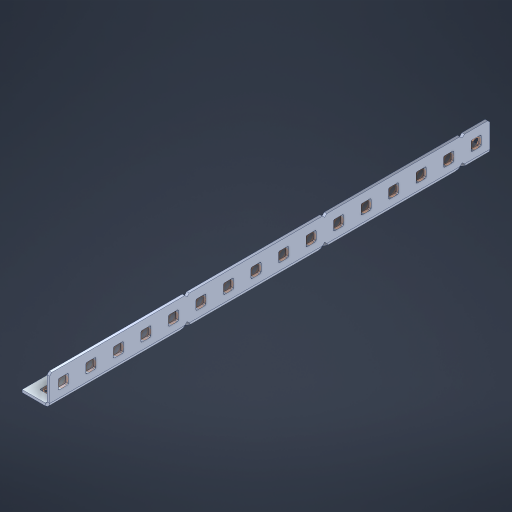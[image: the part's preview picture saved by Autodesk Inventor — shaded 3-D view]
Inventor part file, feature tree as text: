
AUTODESK INVENTOR PART (.ipt)
format: ipt  version: 2023 (Build 270158000, 158)  size: 676,864 bytes
history: native  units: in
note: dims shown in document units (in); Inventor stores cm internally (conversion verified against a paired STEP export)
features: other x37, extrude x31, sheet_metal_op x10, sketch x8, mirror x1, pattern_linear x1, chamfer x1
ambient origin geometry x8: Origin, YZ Plane, XZ Plane, XY Plane, X Axis, Y Axis, Z Axis, Center Point
bodies: Solid1 (feature_tree), Body (feature_tree)
feature tree (89):
  other  "Flange Pattern Plane"
  sheet_metal_op  "Flange Pattern"
  sheet_metal_op  "Body Pattern"
  other  "Arc Length"
  mirror  "Notch Mirror"
  pattern_linear  "Notch Pattern"  Spacing1=0.1875in  [1 undecoded]
  chamfer  "End Chamfer"
  extrude  "Half Cut"  Depth=0.0469in
  sketch  "Sketch1"  dims[d0=2.5in]
  other  "Plate1"
  sketch  "Sketch2"  dims[d1=8.0in]
  other  "Plate2"
  sheet_metal_op  "Bend1"
  sheet_metal_op  "Corner1"
  sketch  "Sketch3"  dims[d2=0.0469in]
  other  "Flange Pattern Sketch"
  sketch  "Sketch7"  dims[d3=0.0469in]
  other  "Srf1"
  other  "Srf2"
  sketch  "Sketch8"  dims[d4=0.0234in]
  sketch  "Sketch9"  dims[d5=0.0938in]
  other  "Srf91"
  sheet_metal_op  "Body Pattern Sketch"
  other  "Srf92"
  sketch  "Sketch13"  dims[d6=0.0469in]
  sketch  "Sketch14"  dims[d7=0.5in d8=90.0deg d9=0.0312in d10=0.1875in d11=0.0469in d12=0.0469in d16=0.182in d17=0.02in d18=0.0469in d19=0.0in d20=0.25in d21=0.25in d46=0.172in d47=1.0in d48=0.0in d49=0.182in d50=0.02in d51=0.25in d52=0.25in d53=0.0469in d54=0.0in d55=0.172in d56=1.0in d57=0.0in d60=6.2992in d62=0.5in d63=0.3937in d65=0.5in d85=0.1227in d86=0.1659in d88=0.04in d89=0.0469in d90=0.0in d91=0.04in d92=0.0491in d95=2.5in d96=0.04in d97=0.25in d98=45.0deg d101=0.0in d102=2.497in d131=0.5in d132=6.2992in d134=0.5in d139=0.5in]
  other  "Srf856"
  other  "Srf1310"
  other  "Srf1311"
  other  "Srf1312"
  other  "Srf1376"
  other  "Srf1377"
  other  "Srf1728"
  other  "Srf1755"
  other  "Srf1878"
  other  "Srf1879"
  other  "Srf1880"
  other  "Srf1881"
  other  "Srf1882"
  other  "Srf1883"
  other  "Srf1884"
  other  "Srf1885"
  other  "Srf1886"
  other  "Srf1887"
  other  "Srf1942"
  other  "Srf1943"
  other  "Srf1944"
  other  "Srf1945"
  other  "Srf1946"
  other  "Srf1947"
  other  "Srf1948"
  other  "Srf1949"
  other  "Srf1950"
  other  "Srf1951"
  sheet_metal_op  "Flange Stamp"
  sheet_metal_op  "Flange Circle"
  sheet_metal_op  "Body Stamp"
  sheet_metal_op  "Body Circle"
  sheet_metal_op  "Notch"
  extrude  "ExtrusionSrf2"  Depth=0.0469in
  extrude  "ExtrusionSrf92"  Depth=0.5in
  extrude  "ExtrusionSrf856"  Depth=0.02in
  extrude  "ExtrusionSrf1310"  Depth=0.0469in
  extrude  "ExtrusionSrf1311"  TaperAngle=0.0deg  [1 undecoded]
  extrude  "ExtrusionSrf1312"  Depth=0.5in
  extrude  "ExtrusionSrf1376"  Depth=0.5in
  extrude  "ExtrusionSrf1377"  Depth=0.5in
  extrude  "ExtrusionSrf1728"  Depth=0.5in TaperAngle=0.0deg
  extrude  "ExtrusionSrf1755"  Depth=0.5in
  extrude  "ExtrusionSrf1878"  Depth=0.02in
  extrude  "ExtrusionSrf1879"  Depth=0.5in
  extrude  "ExtrusionSrf1880"  Depth=0.5in
  extrude  "ExtrusionSrf1881"  Depth=0.0469in
  extrude  "ExtrusionSrf1882"  TaperAngle=0.0deg  [1 undecoded]
  extrude  "ExtrusionSrf1883"  Depth=0.5in
  extrude  "ExtrusionSrf1884"  Depth=0.5in TaperAngle=0.0deg
  extrude  "ExtrusionSrf1885"  Depth=0.5in
  extrude  "ExtrusionSrf1886"  Depth=0.5in
  extrude  "ExtrusionSrf1887"  Depth=0.5in
  extrude  "ExtrusionSrf1942"  Depth=0.5in
  extrude  "ExtrusionSrf1943"  Depth=0.5in
  extrude  "ExtrusionSrf1944"  Depth=0.0469in
  extrude  "ExtrusionSrf1945"  TaperAngle=0.0deg  [1 undecoded]
  extrude  "ExtrusionSrf1946"  Depth=0.5in
  extrude  "ExtrusionSrf1947"  Depth=0.5in
  extrude  "ExtrusionSrf1948"  Depth=0.5in
  extrude  "ExtrusionSrf1949"  Depth=0.5in TaperAngle=45.0deg
  extrude  "ExtrusionSrf1950"  TaperAngle=0.0deg  [1 undecoded]
  extrude  "ExtrusionSrf1951"  Depth=0.5in
note: 5 required parameter values undecoded (feature->parameter linkage not recoverable at this tier; creation-order binding heuristic only, values carry confidence <= 0.55)
